# Revit family: Solo L shower support
name_source: partatom
category: Specialty Equipment
units: mm (PartAtom-declared; Revit-internal decimal feet)

## family parameters
Always vertical = Yes
Cut with Voids When Loaded = No
Part Type = Normal
Room Calculation Point = No
Round Connector Dimension = Use Diameter
Shared = No
Work Plane-Based = No

## types (6) — shared parameters
Manufacturer = Väinö Korpinen Oy
URL = www.korpinen.com
_BIM_Content_Publish_Date_ = 08.07.2021
_Height_ = 1200 mm
_Width_ = 440 mm  [stored 1.44357 ft]

## per-type parameters (varying)
| type | Left_Handed_ | Right_Handed_ | _Color_ |
| 16806WAM | Yes | No | RAL 9016 - White |
| 16806R | Yes | No | RAL 3003 - Red |
| 16806G | Yes | No | RAL 7037 - Grey |
| 16805GAM | No | Yes | RAL 7037 - Grey |
| 163805R | No | Yes | RAL 3003 - Red |
| 16805W | No | Yes | RAL 9016 - White |

note: [stored X ft] marks values corroborated as IEEE doubles in the binary element streams (Revit-internal decimal feet)

## geometry (parser evidence)
native form markers: Sweep x6
no freeform markers — native parametric forms only
